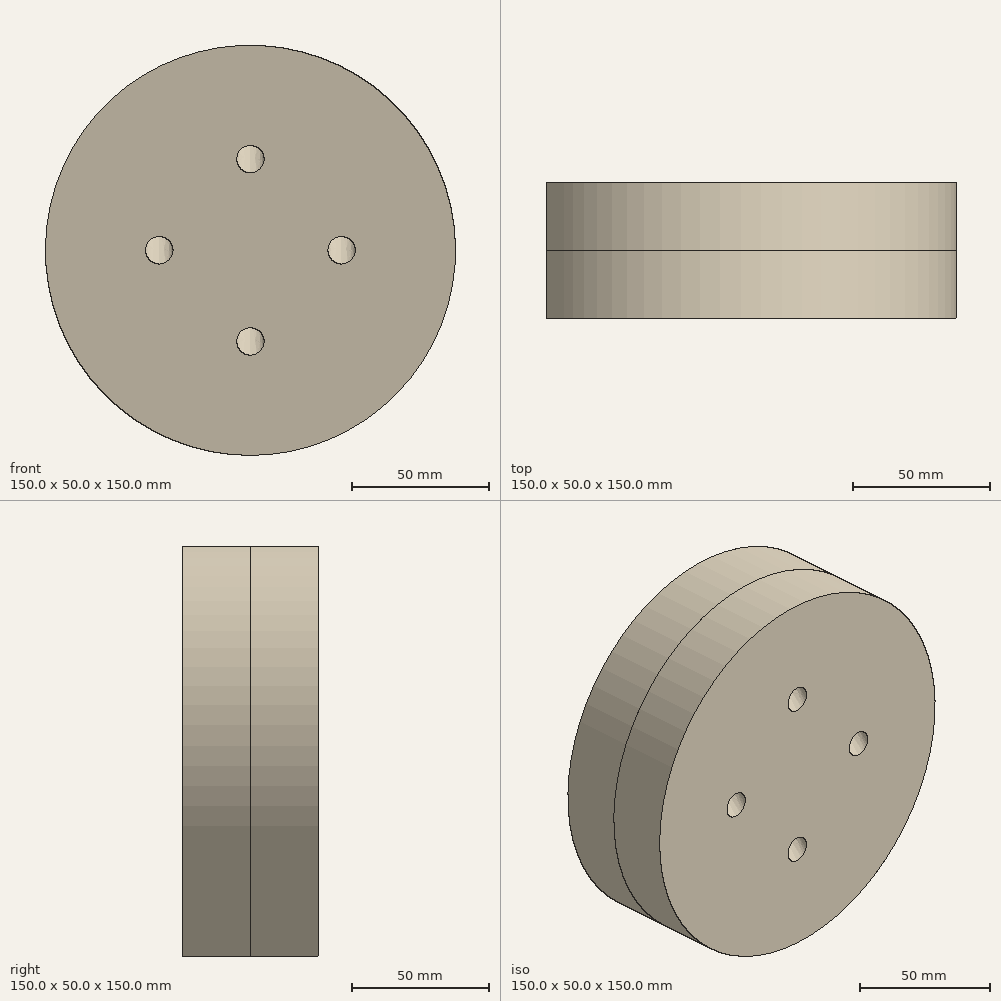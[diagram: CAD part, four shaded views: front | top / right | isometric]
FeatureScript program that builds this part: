
annotation { "Feature Type Name" : "Feature", "Feature Type Description" : "" }
export const myFeature = defineFeature(function(context is Context, id is Id, definition is map)
    precondition{}
    {
        {
            var Q0;
            Q0=qCreatedBy(makeId("Front.planeOp"),FACE);
            var sketch = newSketch(context, id + "F0", { "sketchPlane" : qUnion([Q0])});
            skCircle(sketch, "E0", {"center": v(0, 0) * mm, "radius": 75 * mm});
            skSolve(sketch);
        }
        {
            var Q0;
            Q0 = qSketchRegion(id + "F0", true);
            extrude(context, id + "F1", {"entities" : qUnion([Q0]), "depth" : 25 * mm});
        }
        {
            var Q0;
            Q0=makeQuery(id+"F1.opExtrude","CAP_FACE",FACE,{"disambiguationData":[OSD([sQuery(id+"F0.wireOp",EDGE,"E0")])],"isStart":false});
            var sketch = newSketch(context, id + "F2", { "sketchPlane" : qUnion([Q0])});
            skCircle(sketch, "E1", {"center": v(0, 33.33) * mm, "radius": 5 * mm});
            skCircle(sketch, "E2.1.0", {"center": v(-33.33, 0) * mm, "radius": 5 * mm});
            skCircle(sketch, "E2.2.0", {"center": v(0, -33.33) * mm, "radius": 5 * mm});
            skCircle(sketch, "E2.3.0", {"center": v(33.33, 0) * mm, "radius": 5 * mm});
            skPoint(sketch, "E2.center", {"position": v(0, 0) * mm});
            skSolve(sketch);
        }
        {
            var Q0;
            Q0=qCreatedBy(makeId("Right.planeOp"),FACE);
            var sketch = newSketch(context, id + "F3", { "sketchPlane" : qUnion([Q0])});
            skLineSegment(sketch, "E3", {"start": v(0, 0) * mm, "end": v(-12.06, 13.83) * mm});
            skLineSegment(sketch, "E4", {"start": v(-12.06, 13.83) * mm, "end": v(-25, 0) * mm});
            skSolve(sketch);
        }
        {
            var Q0;
            Q0 = qSketchRegion(id + "F2", true);
            var Q1;
            Q1 = qConstructionFilter(qBodyType(qCreatedBy(id + "F2" ,EDGE), BodyType.WIRE), ConstructionObject.NO);
            var Q2;
            Q2 = qConstructionFilter(qBodyType(qCreatedBy(id + "F3" ,EDGE), BodyType.WIRE), ConstructionObject.NO);
            sweep(context, id + "F4", {"operationType" : NewBodyOperationType.REMOVE, "profiles" : qUnion([Q0]), "surfaceProfiles" : qUnion([Q1]), "path" : qUnion([Q2]), "keepProfileOrientation" : true});
        }
        {
            var Q0;
            Q0=qCreatedBy(makeId("Front.planeOp"),FACE);
            var sketch = newSketch(context, id + "F5", { "sketchPlane" : qUnion([Q0])});
            skCircle(sketch, "E5.0", {"center": v(0, 0) * mm, "radius": 75 * mm});
            skSolve(sketch);
        }
        {
            var Q0;
            Q0 = qSketchRegion(id + "F5", true);
            extrude(context, id + "F6", {"entities" : qUnion([Q0]), "oppositeDirection" : true, "depth" : 25 * mm});
        }
        {
            var Q0;
            Q0=makeQuery(id+"F6.opExtrude","CAP_FACE",FACE,{"disambiguationData":[OSD([sQuery(id+"F5.wireOp",EDGE,"E5.0")])],"isStart":false});
            var sketch = newSketch(context, id + "F7", { "sketchPlane" : qUnion([Q0])});
            skCircle(sketch, "E6.0", {"center": v(-33.33, 0) * mm, "radius": 5 * mm});
            skCircle(sketch, "E6.2", {"center": v(33.33, 0) * mm, "radius": 5 * mm});
            skCircle(sketch, "E6.3", {"center": v(0, 33.33) * mm, "radius": 5 * mm});
            skCircle(sketch, "E7.1", {"center": v(0, -33.33) * mm, "radius": 5 * mm});
            skSolve(sketch);
        }
        {
            var Q0;
            Q0=qCreatedBy(makeId("Top.planeOp"),FACE);
            var sketch = newSketch(context, id + "F8", { "sketchPlane" : qUnion([Q0])});
            skPoint(sketch, "E8.0", {"position": v(33.33, 25) * mm});
            skPoint(sketch, "E8.1", {"position": v(-33.33, 25) * mm});
            skLineSegment(sketch, "E9", {"start": v(33.33, 25) * mm, "end": v(43.33, 12.5) * mm});
            skLineSegment(sketch, "E10", {"start": v(43.33, 12.5) * mm, "end": v(33.33, 0) * mm});
            skLineSegment(sketch, "E11", {"start": v(-33.33, 25) * mm, "end": v(-43.33, 12.5) * mm});
            skLineSegment(sketch, "E12", {"start": v(-43.33, 12.5) * mm, "end": v(-33.33, 0) * mm});
            skSolve(sketch);
        }
        {
            var Q0;
            Q0=qCreatedBy(makeId("Right.planeOp"),FACE);
            var sketch = newSketch(context, id + "F9", { "sketchPlane" : qUnion([Q0])});
            skPoint(sketch, "E13.0", {"position": v(25, 33.33) * mm});
            skPoint(sketch, "E13.1", {"position": v(25, -33.33) * mm});
            skLineSegment(sketch, "E14", {"start": v(25, -33.33) * mm, "end": v(12.5, -43.33) * mm});
            skLineSegment(sketch, "E15", {"start": v(12.5, -43.33) * mm, "end": v(0, -33.33) * mm});
            skLineSegment(sketch, "E16", {"start": v(25, 33.33) * mm, "end": v(12.5, 43.33) * mm});
            skLineSegment(sketch, "E17", {"start": v(12.5, 43.33) * mm, "end": v(0, 33.33) * mm});
            skSolve(sketch);
        }
        {
            var Q0;
            Q0=makeQuery(id+"F7.imprint","IMPRINT",FACE,{"disambiguationData":[TD([[makeQuery(id+"F7.imprint","IMPRINT",EDGE,{"derivedFrom":sQuery(id+"F7.wireOp",EDGE,"E7.1")}),1.0]])]});
            var Q1;
            Q1=sQuery(id+"F9.wireOp",EDGE,"E14");
            var Q2;
            Q2=sQuery(id+"F9.wireOp",EDGE,"E15");
            sweep(context, id + "F10", {"operationType" : NewBodyOperationType.REMOVE, "profiles" : qUnion([Q0]), "path" : qUnion([Q1, Q2])});
        }
        {
            var Q0;
            Q0=makeQuery(id+"F7.imprint","IMPRINT",FACE,{"disambiguationData":[TD([[makeQuery(id+"F7.imprint","IMPRINT",EDGE,{"derivedFrom":sQuery(id+"F7.wireOp",EDGE,"E6.3")}),1.0]])]});
            var Q1;
            Q1=sQuery(id+"F9.wireOp",EDGE,"E16");
            var Q2;
            Q2=sQuery(id+"F9.wireOp",EDGE,"E17");
            sweep(context, id + "F11", {"operationType" : NewBodyOperationType.REMOVE, "profiles" : qUnion([Q0]), "path" : qUnion([Q1, Q2])});
        }
        {
            var Q0;
            Q0=makeQuery(id+"F7.imprint","IMPRINT",FACE,{"disambiguationData":[TD([[makeQuery(id+"F7.imprint","IMPRINT",EDGE,{"derivedFrom":sQuery(id+"F7.wireOp",EDGE,"E6.2")}),1.0]])]});
            var Q1;
            Q1=sQuery(id+"F8.wireOp",EDGE,"E11");
            var Q2;
            Q2=sQuery(id+"F8.wireOp",EDGE,"E12");
            sweep(context, id + "F12", {"operationType" : NewBodyOperationType.REMOVE, "profiles" : qUnion([Q0]), "path" : qUnion([Q1, Q2])});
        }
        {
            var Q0;
            Q0=makeQuery(id+"F7.imprint","IMPRINT",FACE,{"disambiguationData":[TD([[makeQuery(id+"F7.imprint","IMPRINT",EDGE,{"derivedFrom":sQuery(id+"F7.wireOp",EDGE,"E6.0")}),1.0]])]});
            var Q1;
            Q1=sQuery(id+"F8.wireOp",EDGE,"E9");
            var Q2;
            Q2=sQuery(id+"F8.wireOp",EDGE,"E10");
            sweep(context, id + "F13", {"operationType" : NewBodyOperationType.REMOVE, "profiles" : qUnion([Q0]), "path" : qUnion([Q1, Q2])});
        }
    });
